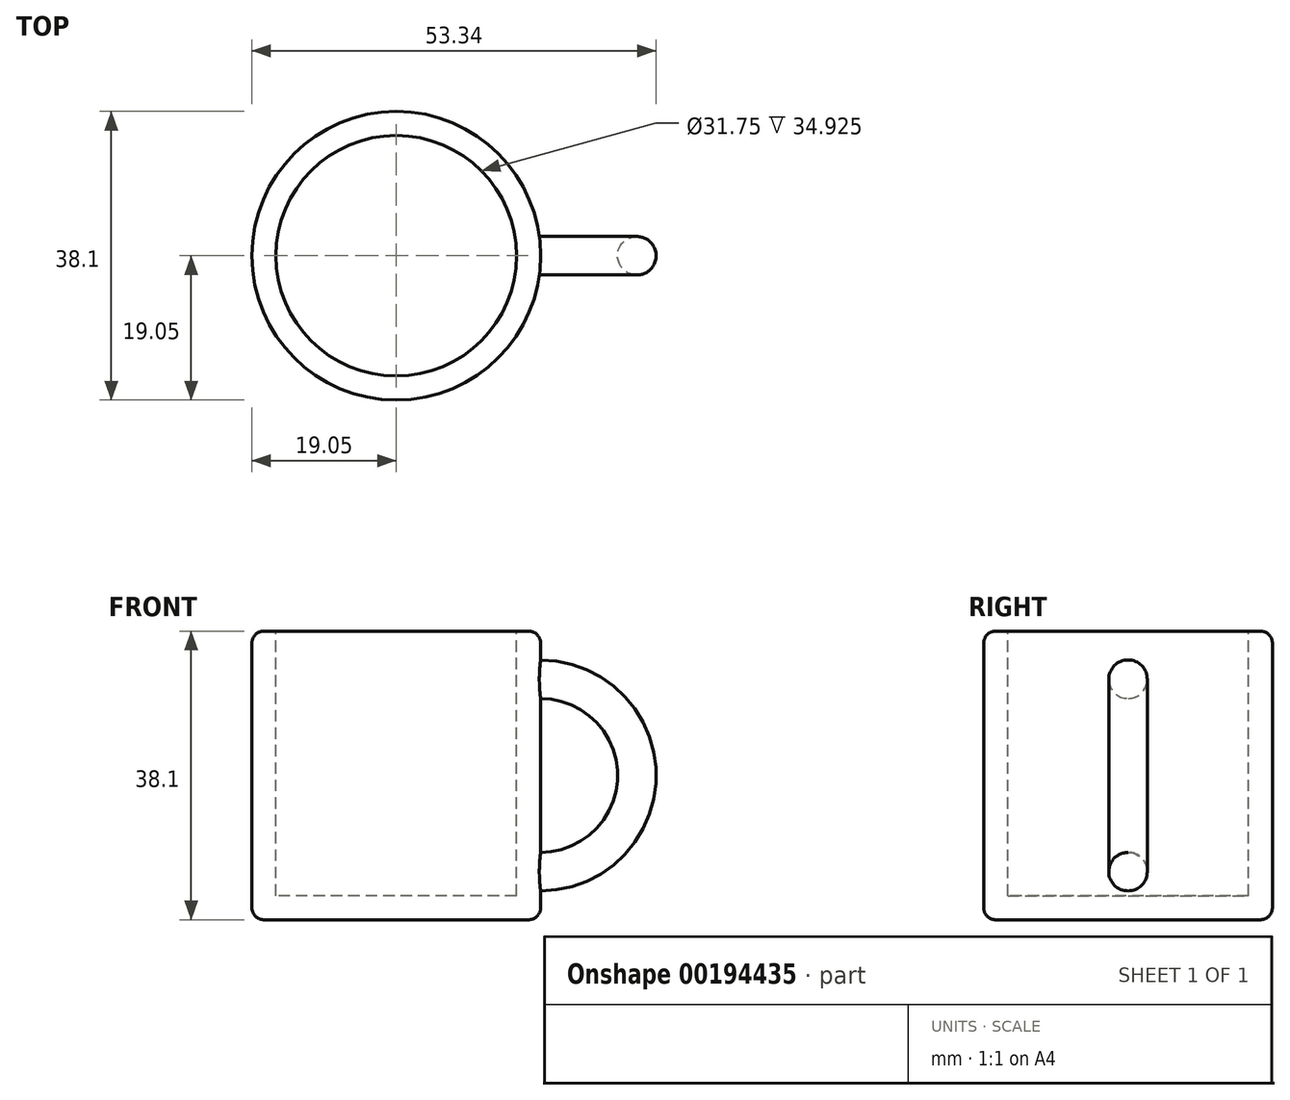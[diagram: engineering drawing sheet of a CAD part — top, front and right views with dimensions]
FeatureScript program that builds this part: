
annotation { "Feature Type Name" : "Feature", "Feature Type Description" : "" }
export const myFeature = defineFeature(function(context is Context, id is Id, definition is map)
    precondition{}
    {
        {
            var Q0;
            Q0=qCreatedBy(makeId("Front.planeOp"),FACE);
            var sketch = newSketch(context, id + "F0", { "sketchPlane" : qUnion([Q0])});
            skLineSegment(sketch, "E0.bottom", {"start": v(0, 0) * mm, "end": v(19.05, 0) * mm});
            skLineSegment(sketch, "E0.top", {"start": v(0, 38.1) * mm, "end": v(19.05, 38.1) * mm});
            skLineSegment(sketch, "E0.left", {"start": v(0, 0) * mm, "end": v(0, 38.1) * mm});
            skLineSegment(sketch, "E0.right", {"start": v(19.05, 0) * mm, "end": v(19.05, 38.1) * mm});
            skSolve(sketch);
        }
        {
            var Q0;
            Q0 = qSketchRegion(id + "F0", true);
            var Q1;
            Q1=sQuery(id+"F0.wireOp",EDGE,"E0.left");
            revolve(context, id + "F1", {"entities" : qUnion([Q0]), "axis" : qUnion([Q1]), "revolveType" : RevolveType.FULL});
        }
        {
            var Q0;
            Q0=makeQuery(id+"F1.opRevolve","SWEPT_FACE",FACE,{"disambiguationData":[OSD([sQuery(id+"F0.wireOp",EDGE,"E0.top")])]});
            var sketch = newSketch(context, id + "F2", { "sketchPlane" : qUnion([Q0])});
            skCircle(sketch, "E1", {"center": v(0, 0) * mm, "radius": 15.88 * mm});
            skSolve(sketch);
        }
        {
            var Q0;
            Q0=makeQuery(id+"F2.imprint","IMPRINT",FACE,{"disambiguationData":[TD([[makeQuery(id+"F2.imprint","IMPRINT",EDGE,{"derivedFrom":sQuery(id+"F2.wireOp",EDGE,"E1")}),1.0]])]});
            extrude(context, id + "F3", {"entities" : qUnion([Q0]), "operationType" : NewBodyOperationType.REMOVE, "oppositeDirection" : true, "depth" : 34.92 * mm});
        }
        {
            var Q0;
            Q0=qCreatedBy(makeId("Right.planeOp"),FACE);
            cPlane(context, id + "F4", {"entities" : qUnion([Q0]), "cplaneType" : CPlaneType.OFFSET, "offset" : 19.05 * mm, "width" : 152.4 * mm, "height" : 152.4 * mm});
        }
        {
            var Q0;
            Q0=qCreatedBy(makeId("Front.planeOp"),FACE);
            var sketch = newSketch(context, id + "F5", { "sketchPlane" : qUnion([Q0])});
            skArc(sketch, "E2", {"start": v(19.05, 6.35) * mm, "mid": v(31.75, 19.05) * mm, "end": v(19.05, 31.75) * mm});
            skSolve(sketch);
        }
        {
            var Q0;
            Q0=makeQuery(id+"F1.opRevolve","SWEPT_EDGE",EDGE,{"disambiguationData":[OSD([sQuery(id+"F0.wireOp",EDGE,"E0.top"),sQuery(id+"F0.wireOp",EDGE,"E0.right")])]});
            var Q1;
            Q1=makeQuery(id+"F3.boolean.opBoolean","COPY",EDGE,{"derivedFrom":makeQuery(id+"F3.opExtrude","CAP_EDGE",EDGE,{"disambiguationData":[OSD([sQuery(id+"F2.wireOp",EDGE,"E1")])],"isStart":true})});
            fillet(context, id + "F6", {"entities" : qUnion([Q0, Q1]), "radius" : 1.59 * mm, "tangentPropagation" : true, "allowEdgeOverflow" : false});
        }
        {
            var Q0;
            Q0=makeQuery(id+"F1.opRevolve","SWEPT_EDGE",EDGE,{"disambiguationData":[OSD([sQuery(id+"F0.wireOp",EDGE,"E0.bottom"),sQuery(id+"F0.wireOp",EDGE,"E0.right")])]});
            fillet(context, id + "F7", {"entities" : qUnion([Q0]), "radius" : 1.59 * mm, "tangentPropagation" : true, "allowEdgeOverflow" : false});
        }
        {
            var Q0;
            Q0=qCreatedBy(id+"F4.planeOp",FACE);
            var sketch = newSketch(context, id + "F8", { "sketchPlane" : qUnion([Q0])});
            skCircle(sketch, "E3", {"center": v(0, 31.75) * mm, "radius": 2.54 * mm});
            skCircle(sketch, "E4", {"center": v(0, 6.35) * mm, "radius": 2.54 * mm});
            skSolve(sketch);
        }
        {
            var Q0;
            Q0=makeQuery(id+"F8.imprint","IMPRINT",FACE,{"disambiguationData":[TD([[makeQuery(id+"F8.imprint","IMPRINT",EDGE,{"derivedFrom":sQuery(id+"F8.wireOp",EDGE,"E3")}),1.0]])]});
            var Q1;
            Q1 = qConstructionFilter(qBodyType(qCreatedBy(id + "F5" ,EDGE), BodyType.WIRE), ConstructionObject.NO);
            sweep(context, id + "F9", {"operationType" : NewBodyOperationType.ADD, "profiles" : qUnion([Q0]), "path" : qUnion([Q1])});
        }
        {
            var Q0;
            Q0=makeQuery(id+"F9.opSweep","CAP_FACE",FACE,{"disambiguationData":[OSD([sQuery(id+"F5.wireOp",VERTEX,"E2.end"),sQuery(id+"F8.wireOp",EDGE,"E3")])],"isStart":true});
            var sketch = newSketch(context, id + "F10", { "sketchPlane" : qUnion([Q0])});
            skCircle(sketch, "E5", {"center": v(0, 31.75) * mm, "radius": 2.54 * mm});
            skSolve(sketch);
        }
        {
            var Q0;
            Q0=makeQuery(id+"F9.opSweep","CAP_FACE",FACE,{"disambiguationData":[OSD([sQuery(id+"F5.wireOp",VERTEX,"E2.start"),sQuery(id+"F8.wireOp",EDGE,"E3")])],"isStart":false});
            var sketch = newSketch(context, id + "F11", { "sketchPlane" : qUnion([Q0])});
            skCircle(sketch, "E6", {"center": v(0, 6.35) * mm, "radius": 2.54 * mm});
            skSolve(sketch);
        }
        {
            var Q0;
            Q0=makeQuery(id+"F10.imprint","IMPRINT",FACE,{"disambiguationData":[TD([[makeQuery(id+"F10.imprint","IMPRINT",EDGE,{"derivedFrom":sQuery(id+"F10.wireOp",EDGE,"E5")}),-1.0]])]});
            var Q1;
            Q1=makeQuery(id+"F11.imprint","IMPRINT",FACE,{"disambiguationData":[TD([[makeQuery(id+"F11.imprint","IMPRINT",EDGE,{"derivedFrom":sQuery(id+"F11.wireOp",EDGE,"E6")}),1.0]])]});
            var Q2;
            Q2=makeQuery(id+"F1.opRevolve","SWEPT_FACE",FACE,{"disambiguationData":[OSD([sQuery(id+"F0.wireOp",EDGE,"E0.right")])]});
            var Q3;
            Q3=makeQuery(id+"F1.opRevolve","SWEPT_BODY",BODY,{"disambiguationData":[OSD([sQuery(id+"F0.wireOp",EDGE,"E0.bottom"),sQuery(id+"F0.wireOp",EDGE,"E0.top"),sQuery(id+"F0.wireOp",EDGE,"E0.left"),sQuery(id+"F0.wireOp",EDGE,"E0.right")])]});
            extrude(context, id + "F12", {"entities" : qUnion([Q0, Q1]), "operationType" : NewBodyOperationType.ADD, "endBound" : BoundingType.UP_TO_NEXT, "endBoundEntityFace" : qUnion([Q2]), "endBoundEntityBody" : qUnion([Q3]), "depth" : 25.4 * mm});
        }
    });
